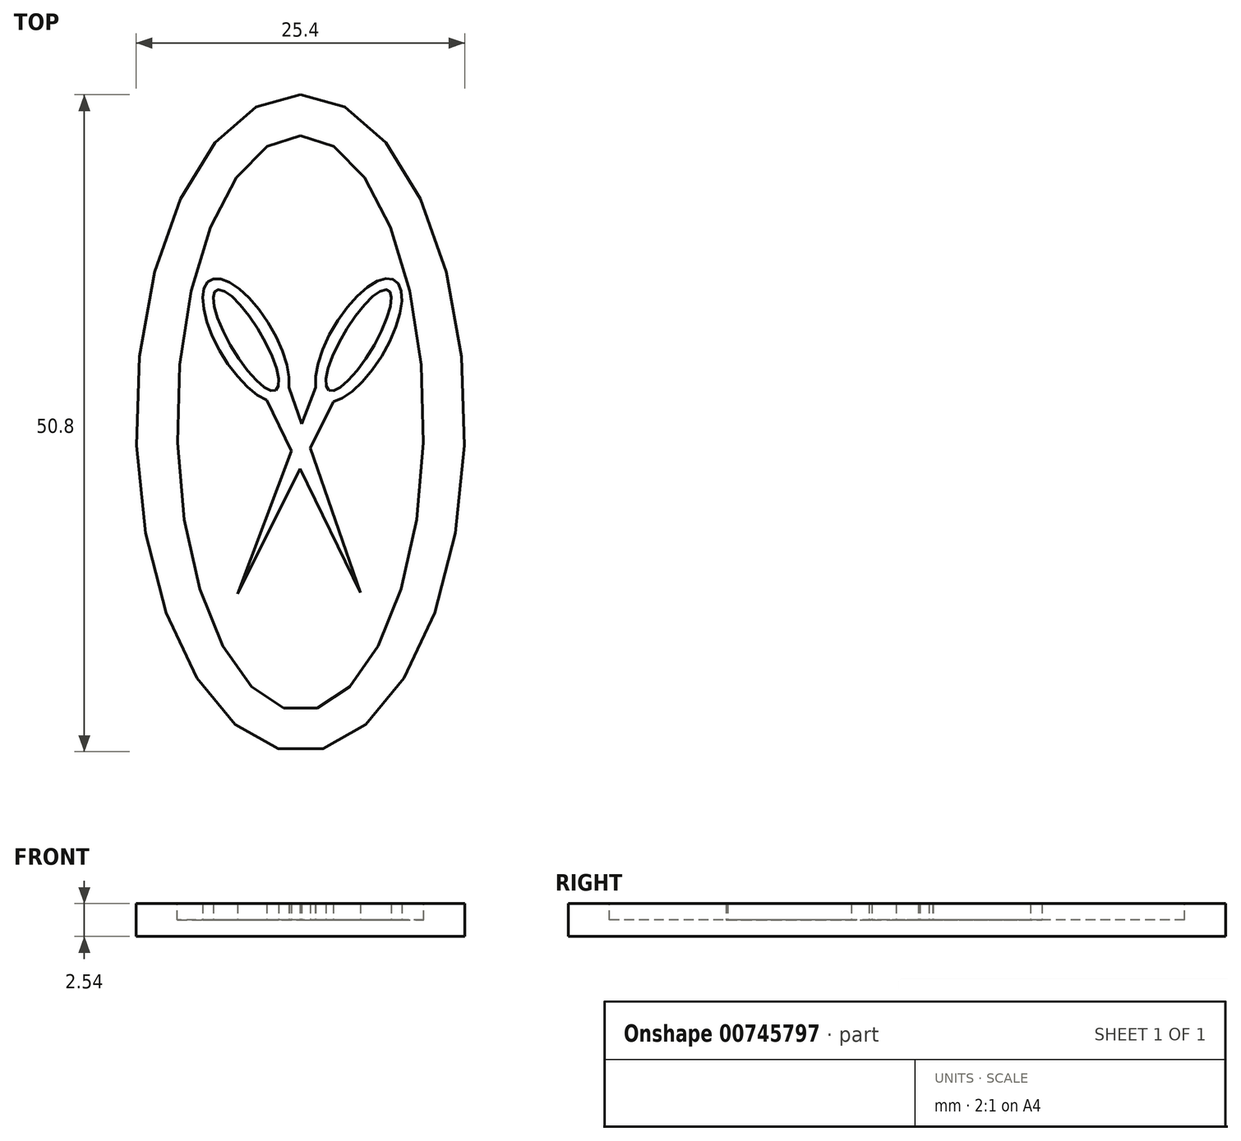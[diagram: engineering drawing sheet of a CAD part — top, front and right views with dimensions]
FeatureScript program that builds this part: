
annotation { "Feature Type Name" : "Feature", "Feature Type Description" : "" }
export const myFeature = defineFeature(function(context is Context, id is Id, definition is map)
    precondition{}
    {
        {
            var Q0;
            Q0=qCreatedBy(makeId("Top.planeOp"),FACE);
            var sketch = newSketch(context, id + "F0", { "sketchPlane" : qUnion([Q0])});
            skEllipse(sketch, "E0", {"center": v(0, 0) * mm, "majorRadius": 25.4 * mm, "minorRadius": 12.7 * mm, "majorAxis": v(0, 1)});
            skSolve(sketch);
        }
        {
            var Q0;
            Q0=qSketchRegion(id+"F0",true);
            extrude(context, id + "F1", {"entities" : qUnion([Q0]), "depth" : 2.54 * mm, "offsetDistance" : 25.4 * mm});
        }
        {
            var Q0;
            Q0=makeQuery(id+"F1.opExtrude","CAP_FACE",FACE,{"disambiguationData":[OSD([sQuery(id+"F0.wireOp",EDGE,"E0")])],"isStart":false});
            var sketch = newSketch(context, id + "F2", { "sketchPlane" : qUnion([Q0])});
            skEllipse(sketch, "E1", {"center": v(0, 0) * mm, "majorRadius": 22.23 * mm, "minorRadius": 9.53 * mm, "majorAxis": v(0, 1)});
            skSolve(sketch);
        }
        {
            var Q0;
            Q0 = qSketchRegion(id + "F2", true);
            extrude(context, id + "F3", {"entities" : qUnion([Q0]), "operationType" : NewBodyOperationType.REMOVE, "oppositeDirection" : true, "depth" : 1.27 * mm, "offsetDistance" : 25.4 * mm});
        }
        {
            var Q0;
            Q0=makeQuery(id+"F3.boolean.opBoolean","COPY",FACE,{"derivedFrom":makeQuery(id+"F3.opExtrude","CAP_FACE",FACE,{"disambiguationData":[OSD([sQuery(id+"F2.wireOp",EDGE,"E1")])],"isStart":false})});
            var sketch = newSketch(context, id + "F4", { "sketchPlane" : qUnion([Q0])});
            skLineSegment(sketch, "E2", {"start": v(-2.62, 1.78) * mm, "end": v(4.63, -13.1) * mm});
            skLineSegment(sketch, "E3", {"start": v(4.63, -13.1) * mm, "end": v(-0.88, 2.76) * mm});
            skEllipse(sketch, "E4", {"center": v(4.49, 6.4) * mm, "majorRadius": 5.42 * mm, "minorRadius": 2.17 * mm, "majorAxis": v(-0.51, -0.86)});
            skEllipse(sketch, "E5", {"center": v(4.49, 6.4) * mm, "majorRadius": 4.5 * mm, "minorRadius": 1.24 * mm, "majorAxis": v(-0.51, -0.86)});
            skLineSegment(sketch, "E6", {"start": v(-4.86, -13.2) * mm, "end": v(2.55, 1.66) * mm});
            skLineSegment(sketch, "E7", {"start": v(-4.86, -13.2) * mm, "end": v(1.16, 2.78) * mm});
            skEllipse(sketch, "E8.MirrorC", {"center": v(-4.2, 6.4) * mm, "majorRadius": 4.5 * mm, "minorRadius": 1.24 * mm, "majorAxis": v(0.51, -0.86)});
            skEllipse(sketch, "E9.MirrorC", {"center": v(-4.2, 6.4) * mm, "majorRadius": 5.42 * mm, "minorRadius": 2.17 * mm, "majorAxis": v(0.51, -0.86)});
            skSolve(sketch);
        }
        {
            var Q0;
            Q0 = qSketchRegion(id + "F4", true);
            extrude(context, id + "F5", {"entities" : qUnion([Q0]), "operationType" : NewBodyOperationType.ADD, "depth" : 1.27 * mm, "offsetDistance" : 25.4 * mm});
        }
    });
